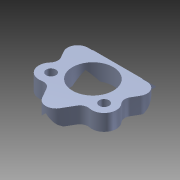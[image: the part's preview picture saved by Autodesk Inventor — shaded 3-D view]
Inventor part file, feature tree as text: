
AUTODESK INVENTOR PART (.ipt)
format: ipt  version: 2011 (Build 150239000, 239)  size: 576,000 bytes
history: native  units: in
note: dims shown in document units (in); Inventor stores cm internally (conversion verified against a paired STEP export)
features: sketch x4, hole x2, other x1, imported_body x1, extrude x1, draft x1, emboss x1, fillet x1
ambient origin geometry x8: Origin, YZ Plane, XZ Plane, XY Plane, X Axis, Y Axis, Z Axis, Center Point
feature tree (12):
  other  "TricornerSeat"
  imported_body  "Base1"
  extrude  "Extrusion1"  TaperAngle=45.0deg  [1 undecoded]
  draft  "FaceDraft1"
  emboss  "Emboss1"
  sketch  "Sketch4"  dims[d21=0.0394in d22=0.0394in d23=0.002in]
  sketch  "Sketch5"  dims[d24=0.002in d25=3.937in d27=0.0394in d28=1.9685in d30=0.0394in d33=0.0039in d34=0.0in d35=0.0945in d36=0.2362in d37=0.1732in d38=0.0787in d39=90.0deg d40=0.315in d41=0.8108in d42=0.0945in d43=0.2362in d44=0.1732in d45=0.0787in d46=90.0deg d47=0.315in d48=0.8108in d49=0.0394in]
  hole  "Hole1"  [1 undecoded]
  hole  "Hole2"  [1 undecoded]
  fillet  "Fillet1"  Radius=0.002in
  sketch  "Sketch1"  dims[d0=0.0039in d1=0.0in d2=45.0deg]
  sketch  "Sketch3"  dims[d19=0.1969in d20=0.0984in]
note: 3 required parameter values undecoded (feature->parameter linkage not recoverable at this tier; creation-order binding heuristic only, values carry confidence <= 0.55)
